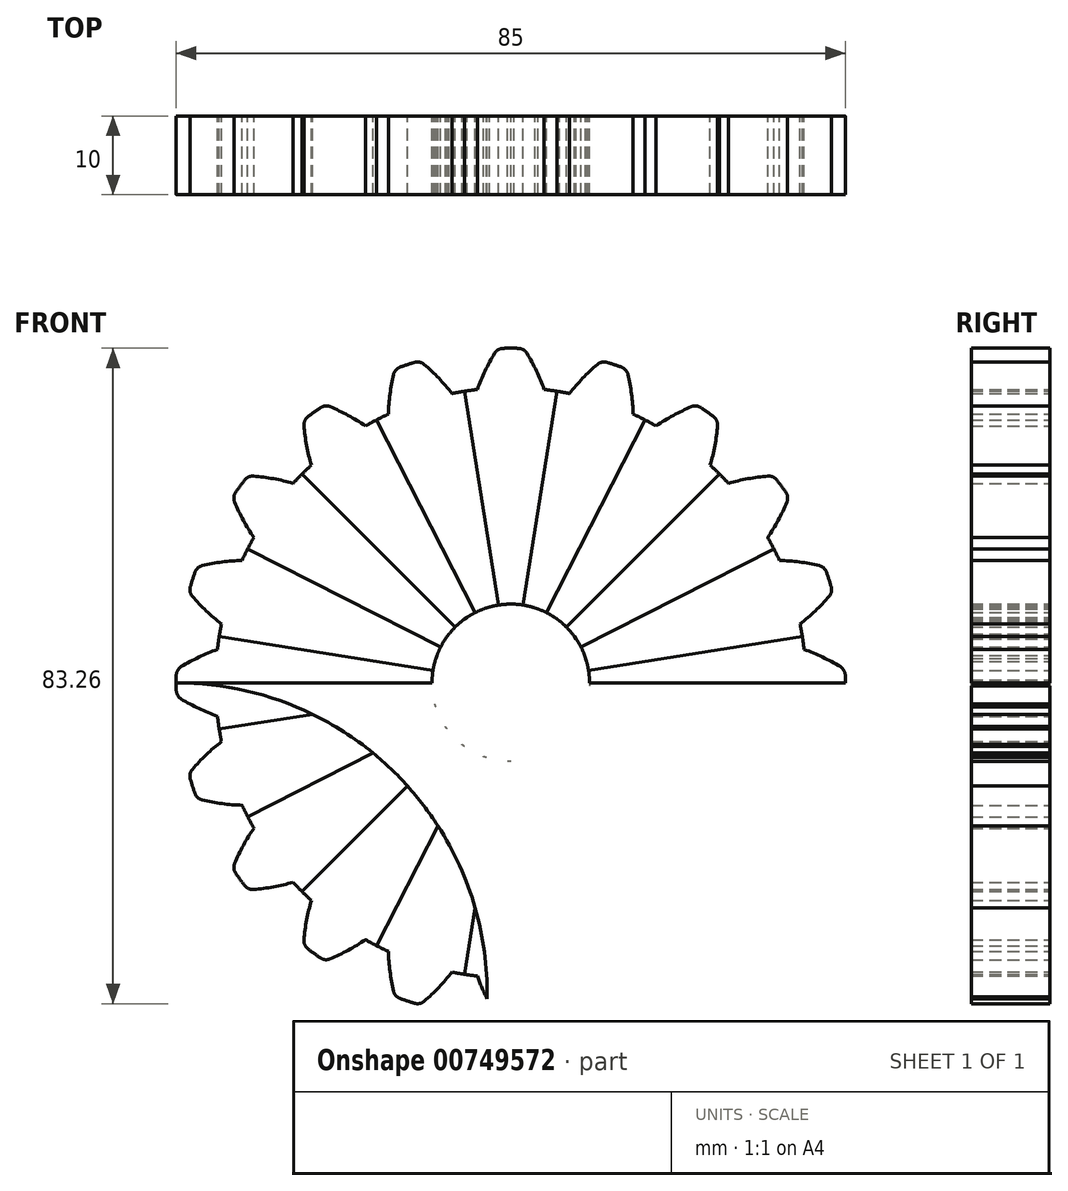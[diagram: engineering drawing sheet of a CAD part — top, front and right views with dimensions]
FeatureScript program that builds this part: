
annotation { "Feature Type Name" : "Feature", "Feature Type Description" : "" }
export const myFeature = defineFeature(function(context is Context, id is Id, definition is map)
    precondition{}
    {
        {
            var Q0;
            Q0=qCreatedBy(makeId("Front.planeOp"),FACE);
            var sketch = newSketch(context, id + "F0", { "sketchPlane" : qUnion([Q0])});
            skCircle(sketch, "E0", {"center": v(0, 0) * mm, "radius": 37.5 * mm, "construction": true});
            skArc(sketch, "E1", {"start": v(1.56, 9.88) * mm, "mid": v(0.98, 9.95) * mm, "end": v(0.4, 10) * mm});
            skCircle(sketch, "E2", {"center": v(0, 0) * mm, "radius": 40 * mm, "construction": true});
            skCircle(sketch, "E3", {"center": v(0, 0) * mm, "radius": 42.5 * mm, "construction": true});
            skLineSegment(sketch, "E4", {"start": v(0, 0) * mm, "end": v(0, 42.5) * mm, "construction": true});
            skLineSegment(sketch, "E5", {"start": v(0, 0) * mm, "end": v(1.67, 42.47) * mm, "construction": true});
            skLineSegment(sketch, "E6", {"start": v(0, 0) * mm, "end": v(4.81, 42.23) * mm, "construction": true});
            skLineSegment(sketch, "E7", {"start": v(0, 0) * mm, "end": v(6.65, 41.98) * mm, "construction": true});
            skArc(sketch, "E8", {"start": v(5.87, 37.04) * mm, "mid": v(5.06, 37.16) * mm, "end": v(4.25, 37.26) * mm});
            skArc(sketch, "E9", {"start": v(0.97, 42.49) * mm, "mid": v(0.48, 42.5) * mm, "end": v(0, 42.5) * mm});
            skArc(sketch, "E10", {"start": v(4.25, 37.26) * mm, "mid": v(3.26, 39.62) * mm, "end": v(2.05, 41.87) * mm});
            skArc(sketch, "E11.MirrorCS", {"start": v(-0.97, 42.49) * mm, "mid": v(-0.48, 42.5) * mm, "end": v(0, 42.5) * mm});
            skArc(sketch, "E12.MirrorCS", {"start": v(-4.25, 37.26) * mm, "mid": v(-3.26, 39.62) * mm, "end": v(-2.05, 41.87) * mm});
            skArc(sketch, "E13.MirrorCS", {"start": v(-5.87, 37.04) * mm, "mid": v(-5.06, 37.16) * mm, "end": v(-4.25, 37.26) * mm});
            skLineSegment(sketch, "E14", {"start": v(-1.56, 9.88) * mm, "end": v(-5.87, 37.04) * mm});
            skLineSegment(sketch, "E15", {"start": v(1.56, 9.88) * mm, "end": v(5.87, 37.04) * mm});
            skPoint(sketch, "E16.visualSharp", {"position": v(1.67, 42.47) * mm});
            skArc(sketch, "E16.filletArc", {"start": v(2.05, 41.87) * mm, "mid": v(1.59, 42.32) * mm, "end": v(0.97, 42.49) * mm});
            skPoint(sketch, "E17.visualSharp", {"position": v(-1.67, 42.47) * mm});
            skArc(sketch, "E17.filletArc", {"start": v(-0.97, 42.49) * mm, "mid": v(-1.59, 42.32) * mm, "end": v(-2.05, 41.87) * mm});
            skCircle(sketch, "E18", {"center": v(0, -40) * mm, "radius": 1.5 * mm});
            skArc(sketch, "E19", {"start": v(-3, -39.89) * mm, "mid": v(0, -43) * mm, "end": v(3, -39.89) * mm});
            skLineSegment(sketch, "E20", {"start": v(-42.5, 0) * mm, "end": v(-10, 0) * mm});
            skArc(sketch, "E21", {"start": v(42.5, 0) * mm, "mid": v(14.43, -11.7) * mm, "end": v(3, -39.89) * mm});
            skArc(sketch, "E22.MirrorCS", {"start": v(-42.5, 0) * mm, "mid": v(-14.43, -11.7) * mm, "end": v(-3, -39.89) * mm});
            skArc(sketch, "E23", {"start": v(-42.5, 0) * mm, "mid": v(0, -43) * mm, "end": v(42.5, 0) * mm});
            skArc(sketch, "E24", {"start": v(-10, 0) * mm, "mid": v(0, -10) * mm, "end": v(10, 0) * mm});
            skArc(sketch, "E25.trimOffspring", {"start": v(0, 10) * mm, "mid": v(-0.78, 9.97) * mm, "end": v(-1.56, 9.88) * mm});
            skLineSegment(sketch, "E26", {"start": v(0, 10) * mm, "end": v(0.4, 10) * mm});
            skLineSegment(sketch, "E27.trimOffspring", {"start": v(10, 0) * mm, "end": v(42.5, 0) * mm});
            skSolve(sketch);
        }
        {
            var Q0;
            Q0=makeQuery(id+"F0.imprint","IMPRINT",FACE,{"disambiguationData":[TD([[makeQuery(id+"F0.imprint","IMPRINT",EDGE,{"derivedFrom":sQuery(id+"F0.wireOp",EDGE,"E1")}),-1.0]])]});
            extrude(context, id + "F1", {"entities" : qUnion([Q0]), "depth" : 10 * mm, "offsetDistance" : 25 * mm});
        }
        {
            var Q0;
            Q0=makeQuery(id+"F1.opExtrude","SWEPT_BODY",BODY,{"disambiguationData":[OSD([sQuery(id+"F0.wireOp",EDGE,"E1"),sQuery(id+"F0.wireOp",EDGE,"E8"),sQuery(id+"F0.wireOp",EDGE,"E9"),sQuery(id+"F0.wireOp",EDGE,"E10"),sQuery(id+"F0.wireOp",EDGE,"E11.MirrorCS"),sQuery(id+"F0.wireOp",EDGE,"E12.MirrorCS"),sQuery(id+"F0.wireOp",EDGE,"E13.MirrorCS"),sQuery(id+"F0.wireOp",EDGE,"E14"),sQuery(id+"F0.wireOp",EDGE,"E15")])]});
            var Q1;
            Q1=makeQuery(id+"F1.opExtrude","SWEPT_FACE",FACE,{"disambiguationData":[OSD([sQuery(id+"F0.wireOp",EDGE,"E1")])]});
            circularPattern(context, id + "F2", {"entities" : qUnion([Q0]), "axis" : qUnion([Q1]), "angle" : 360 * degree, "instanceCount" : 20, "equalSpace" : true, "isCentered" : true});
        }
        {
            var Q0;
            {var subQ0=sQuery(id+"F0.wireOp",EDGE,"E22.MirrorCS");Q0=makeQuery(id+"F0.imprint","IMPRINT",FACE,{"disambiguationData":[TD([[makeQuery(id+"F0.imprint","IMPRINT",EDGE,{"derivedFrom":subQ0}),-1.0]])]});}
            var Q1;
            {var subQ0=sQuery(id+"F0.wireOp",EDGE,"E21");Q1=makeQuery(id+"F0.imprint","IMPRINT",FACE,{"disambiguationData":[TD([[makeQuery(id+"F0.imprint","IMPRINT",EDGE,{"derivedFrom":subQ0}),1.0]])]});}
            var Q2;
            Q2=makeQuery(id+"F0.imprint","IMPRINT",FACE,{"disambiguationData":[TD([[makeQuery(id+"F0.imprint","IMPRINT",EDGE,{"derivedFrom":sQuery(id+"F0.wireOp",EDGE,"E18")}),1.0]])]});
            extrude(context, id + "F3", {"entities" : qUnion([Q0, Q1, Q2]), "operationType" : NewBodyOperationType.REMOVE, "depth" : 25 * mm, "offsetDistance" : 25 * mm});
        }
    });
